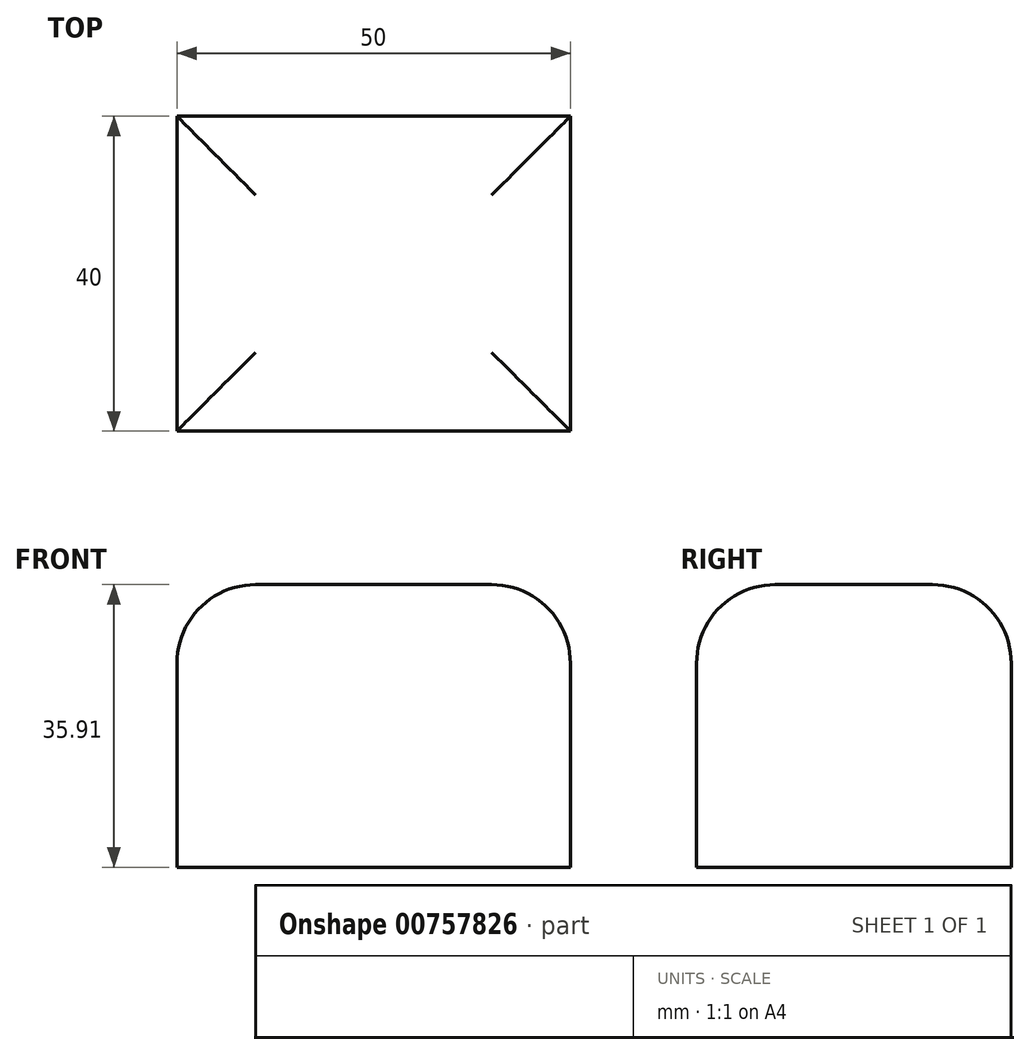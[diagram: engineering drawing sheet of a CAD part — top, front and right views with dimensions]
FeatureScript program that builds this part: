
annotation { "Feature Type Name" : "Feature", "Feature Type Description" : "" }
export const myFeature = defineFeature(function(context is Context, id is Id, definition is map)
    precondition{}
    {
        {
            var Q0;
            Q0=qCreatedBy(makeId("Top.planeOp"),FACE);
            var sketch = newSketch(context, id + "F0", { "sketchPlane" : qUnion([Q0])});
            skLineSegment(sketch, "E0.bottom", {"start": v(-21.68, -16.92) * mm, "end": v(28.32, -16.92) * mm});
            skLineSegment(sketch, "E0.top", {"start": v(-21.68, 23.08) * mm, "end": v(28.32, 23.08) * mm});
            skLineSegment(sketch, "E0.left", {"start": v(-21.68, -16.92) * mm, "end": v(-21.68, 23.08) * mm});
            skLineSegment(sketch, "E0.right", {"start": v(28.32, -16.92) * mm, "end": v(28.32, 23.08) * mm});
            skSolve(sketch);
        }
        {
            var Q0;
            Q0 = qSketchRegion(id + "F0", true);
            extrude(context, id + "F1", {"entities" : qUnion([Q0]), "depth" : 35.9 * mm, "offsetDistance" : 25 * mm});
        }
        {
            var Q0;
            Q0=makeQuery(id+"F1.opExtrude","CAP_EDGE",EDGE,{"disambiguationData":[OSD([sQuery(id+"F0.wireOp",EDGE,"E0.right")])],"isStart":false});
            var Q1;
            Q1=makeQuery(id+"F1.opExtrude","CAP_EDGE",EDGE,{"disambiguationData":[OSD([sQuery(id+"F0.wireOp",EDGE,"E0.bottom")])],"isStart":false});
            var Q2;
            Q2=makeQuery(id+"F1.opExtrude","CAP_EDGE",EDGE,{"disambiguationData":[OSD([sQuery(id+"F0.wireOp",EDGE,"E0.top")])],"isStart":false});
            var Q3;
            Q3=makeQuery(id+"F1.opExtrude","CAP_EDGE",EDGE,{"disambiguationData":[OSD([sQuery(id+"F0.wireOp",EDGE,"E0.left")])],"isStart":false});
            fillet(context, id + "F2", {"entities" : qUnion([Q0, Q1, Q2, Q3]), "radius" : 10 * mm, "tangentPropagation" : true, "allowEdgeOverflow" : false});
        }
    });
